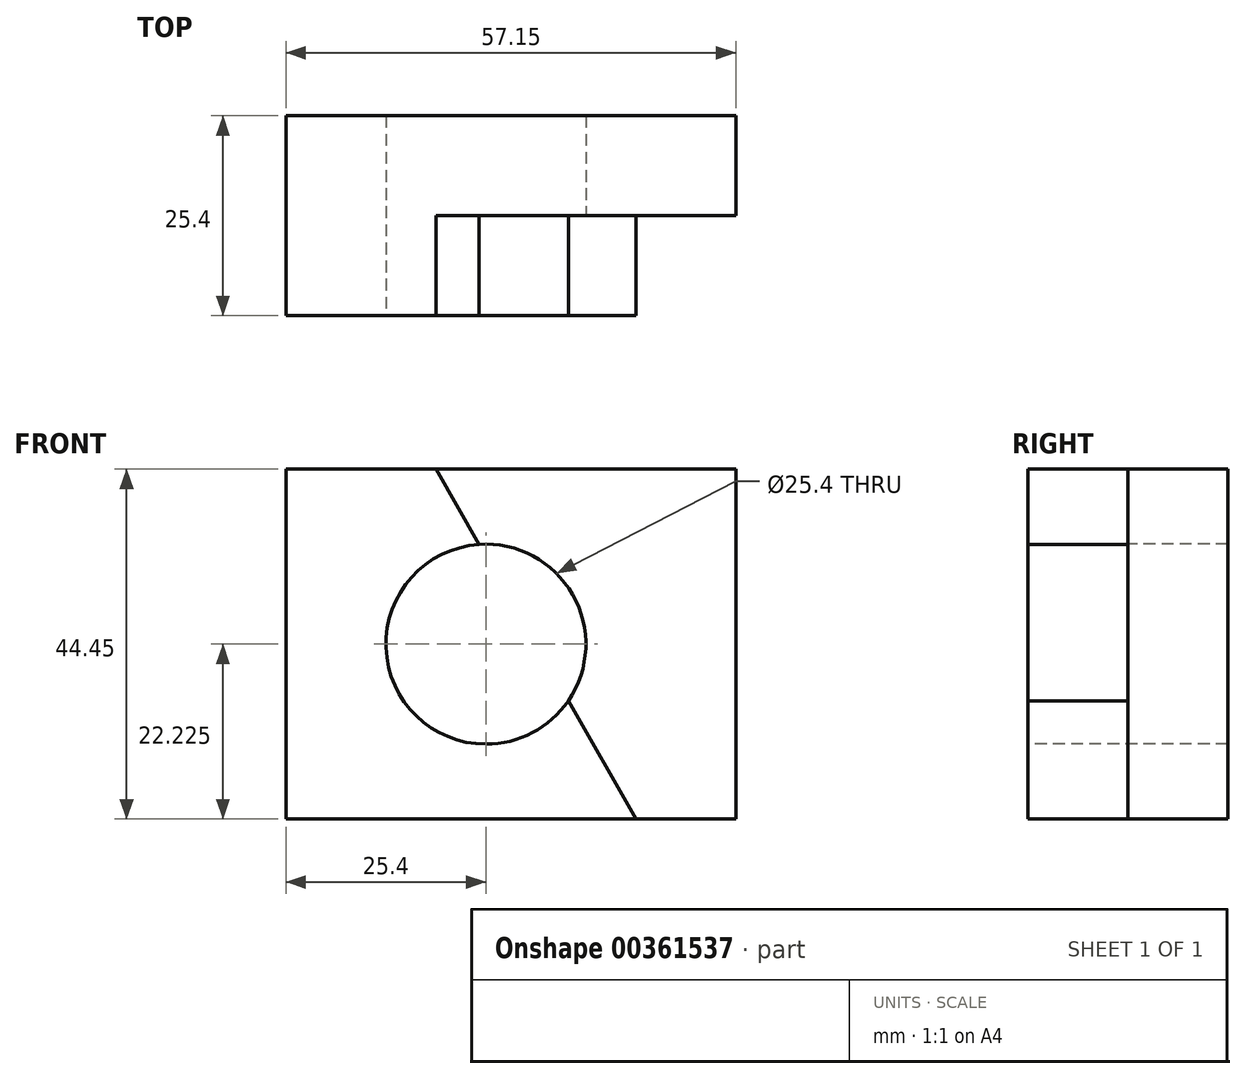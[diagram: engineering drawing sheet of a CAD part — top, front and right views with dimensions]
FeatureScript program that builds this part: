
annotation { "Feature Type Name" : "Feature", "Feature Type Description" : "" }
export const myFeature = defineFeature(function(context is Context, id is Id, definition is map)
    precondition{}
    {
        {
            var Q0;
            Q0=qCreatedBy(makeId("Front.planeOp"),FACE);
            var sketch = newSketch(context, id + "F0", { "sketchPlane" : qUnion([Q0])});
            skLineSegment(sketch, "E0.bottom", {"start": v(0, 44.45) * mm, "end": v(57.15, 44.45) * mm});
            skLineSegment(sketch, "E0.top", {"start": v(0, 0) * mm, "end": v(57.15, 0) * mm});
            skLineSegment(sketch, "E0.left", {"start": v(0, 44.45) * mm, "end": v(0, 0) * mm});
            skLineSegment(sketch, "E0.right", {"start": v(57.15, 44.45) * mm, "end": v(57.15, 0) * mm});
            skSolve(sketch);
        }
        {
            var Q0;
            Q0 = qSketchRegion(id + "F0", true);
            extrude(context, id + "F1", {"entities" : qUnion([Q0]), "depth" : 25.4 * mm});
        }
        {
            var Q0;
            Q0=makeQuery(id+"F1.opExtrude","CAP_FACE",FACE,{"disambiguationData":[OSD([sQuery(id+"F0.wireOp",EDGE,"E0.bottom"),sQuery(id+"F0.wireOp",EDGE,"E0.top"),sQuery(id+"F0.wireOp",EDGE,"E0.left"),sQuery(id+"F0.wireOp",EDGE,"E0.right")])],"isStart":false});
            var sketch = newSketch(context, id + "F2", { "sketchPlane" : qUnion([Q0])});
            skLineSegment(sketch, "E1", {"start": v(44.45, 44.45) * mm, "end": v(44.45, 0) * mm});
            skLineSegment(sketch, "E2", {"start": v(44.45, 0) * mm, "end": v(57.15, 0) * mm});
            skLineSegment(sketch, "E3", {"start": v(57.15, 0) * mm, "end": v(57.15, 44.45) * mm});
            skLineSegment(sketch, "E4", {"start": v(57.15, 44.45) * mm, "end": v(44.45, 44.45) * mm});
            skSolve(sketch);
        }
        {
            var Q0;
            Q0 = qSketchRegion(id + "F2", true);
            extrude(context, id + "F3", {"entities" : qUnion([Q0]), "operationType" : NewBodyOperationType.REMOVE, "oppositeDirection" : true, "depth" : 12.7 * mm});
        }
        {
            var Q0;
            Q0=makeQuery(id+"F1.opExtrude","CAP_FACE",FACE,{"disambiguationData":[OSD([sQuery(id+"F0.wireOp",EDGE,"E0.bottom"),sQuery(id+"F0.wireOp",EDGE,"E0.top"),sQuery(id+"F0.wireOp",EDGE,"E0.left"),sQuery(id+"F0.wireOp",EDGE,"E0.right")])],"isStart":false});
            var sketch = newSketch(context, id + "F4", { "sketchPlane" : qUnion([Q0])});
            skLineSegment(sketch, "E5", {"start": v(44.45, 0) * mm, "end": v(44.45, 44.45) * mm});
            skLineSegment(sketch, "E6", {"start": v(44.45, 44.45) * mm, "end": v(19.05, 44.45) * mm});
            skLineSegment(sketch, "E7", {"start": v(19.05, 44.45) * mm, "end": v(44.45, 0) * mm});
            skSolve(sketch);
        }
        {
            var Q0;
            Q0=makeQuery(id+"F4.imprint","IMPRINT",FACE,{"disambiguationData":[TD([[makeQuery(id+"F4.imprint","IMPRINT",EDGE,{"derivedFrom":sQuery(id+"F4.wireOp",EDGE,"E5")}),-1.0]])]});
            extrude(context, id + "F5", {"entities" : qUnion([Q0]), "operationType" : NewBodyOperationType.REMOVE, "oppositeDirection" : true, "depth" : 12.7 * mm});
        }
        {
            var Q0;
            Q0=makeQuery(id+"F1.opExtrude","CAP_FACE",FACE,{"disambiguationData":[OSD([sQuery(id+"F0.wireOp",EDGE,"E0.bottom"),sQuery(id+"F0.wireOp",EDGE,"E0.top"),sQuery(id+"F0.wireOp",EDGE,"E0.left"),sQuery(id+"F0.wireOp",EDGE,"E0.right")])],"isStart":false});
            var sketch = newSketch(context, id + "F6", { "sketchPlane" : qUnion([Q0])});
            skCircle(sketch, "E8", {"center": v(25.4, 22.23) * mm, "radius": 12.7 * mm});
            skPoint(sketch, "E8.centerSnap0", {"position": v(31.75, 22.23) * mm});
            skSolve(sketch);
        }
        {
            var Q0;
            Q0 = qSketchRegion(id + "F6", true);
            extrude(context, id + "F7", {"entities" : qUnion([Q0]), "operationType" : NewBodyOperationType.REMOVE, "oppositeDirection" : true, "depth" : 25.4 * mm});
        }
    });
